# Revit family: Tub_Filler-Wall_Mounted-Waterworks-Flyte
name_source: partatom
category: Plumbing Fixtures
revit_build: Autodesk Revit MEP 2014 (Build: 20140709_2115(x64)
units: mm (PartAtom-declared; Revit-internal decimal feet)

## types (4) — shared parameters
ADA Compliant = Yes
Assembly Code = D2010
CW Connection = Yes
Certification IAPMO = Yes
Certification State of MA = Yes
Certification cUPC = Yes
Code Compliance = Code # FLTU30:
Cold Water Connector = Cold Water - Female NPT
Cold Water Diameter = 0' - 0 3/4"
Default Elevation = 2' - 10"
Depth = 0' - 11 5/16"
Fittings Hole Diameter = 0' - 1 1/4"
HW Connection = Yes
Handle Spread = 0' - 10 7/16"
Handshower / Spray Hose Length = 4' - 11"
Height = 0' - 5"
Hot Limit Safety Stop = No
Hot Water Connector = Hot Water - Female NPT
Hot Water Diameter = 0' - 0 3/4"
Inlet Supply Spread = 0' - 5 7/8"
Keynote = 22 40 00
Length = 0' - 11 1/4"
Manufacturer = Waterworks
Model = FLXT30
Pressure = 45.00 psi
Product Documentation Link = http://assets.waterworks.com
Product Page URL = http://www.waterworks.com
Spout Reach = 0' - 11 1/4"
URL = http://www.waterworks.com
Valve Material = Ceramic
Vent Connection = No
Version = 2014 - v1.0a
Warranty = http://www.waterworks.com
Waste Connection = No
Water Pressure = Max: 85psi / Min: 20psi / Recommended: 45psi
‌Installation Requirements or Notes = Standard flow rate 2.0gpm. Also available in high efficient flow options
zero-valued in all types: CWFU, HWFU, WFU

## per-type parameters (varying)
| type | Constraint | Description | Finish | Model SKU | Product Name |
| Chrome | 1 | Exposed Wall Mounted Tub Filler With Handshower and Metal Lever Handles in Chrome, Fixed Spray | Metal - Waterworks - Chrome | 09-91759-36262 | Flyte Exposed Wall Mounted Tub Filler With Handshower and Metal Lever Handles in Chrome |
| Graphite | 2 | Exposed Wall Mounted Tub Filler With Handshower and Metal Lever Handles in Graphite, Fixed Spray | Metal - Waterworks - Graphite | 09-41718-63626 | Flyte Exposed Wall Mounted Tub Filler With Handshower and Metal Lever Handles in Graphite |
| Nickel | 3 | Exposed Wall Mounted Tub Filler With Handshower and Metal Lever Handles in Nickel, Fixed Spray | Metal - Waterworks - Nickel | 09-38781-26409 | Flyte Exposed Wall Mounted Tub Filler With Handshower and Metal Lever Handles in Nickel |
| Unlacquered Brass | 4 | Exposed Wall Mounted Tub Filler With Handshower and Metal Lever Handles in Unlacquered Brass, Fixed Spray | Metal - Waterworks - Unlacquered Brass | 09-30146-35666 | Flyte Wall Mounted Exposed Tub Filler with Handshower and Metal Lever Handles in Unlacquered Brass |

## geometry (parser evidence)
native form markers: Sweep x1
no freeform markers — native parametric forms only
